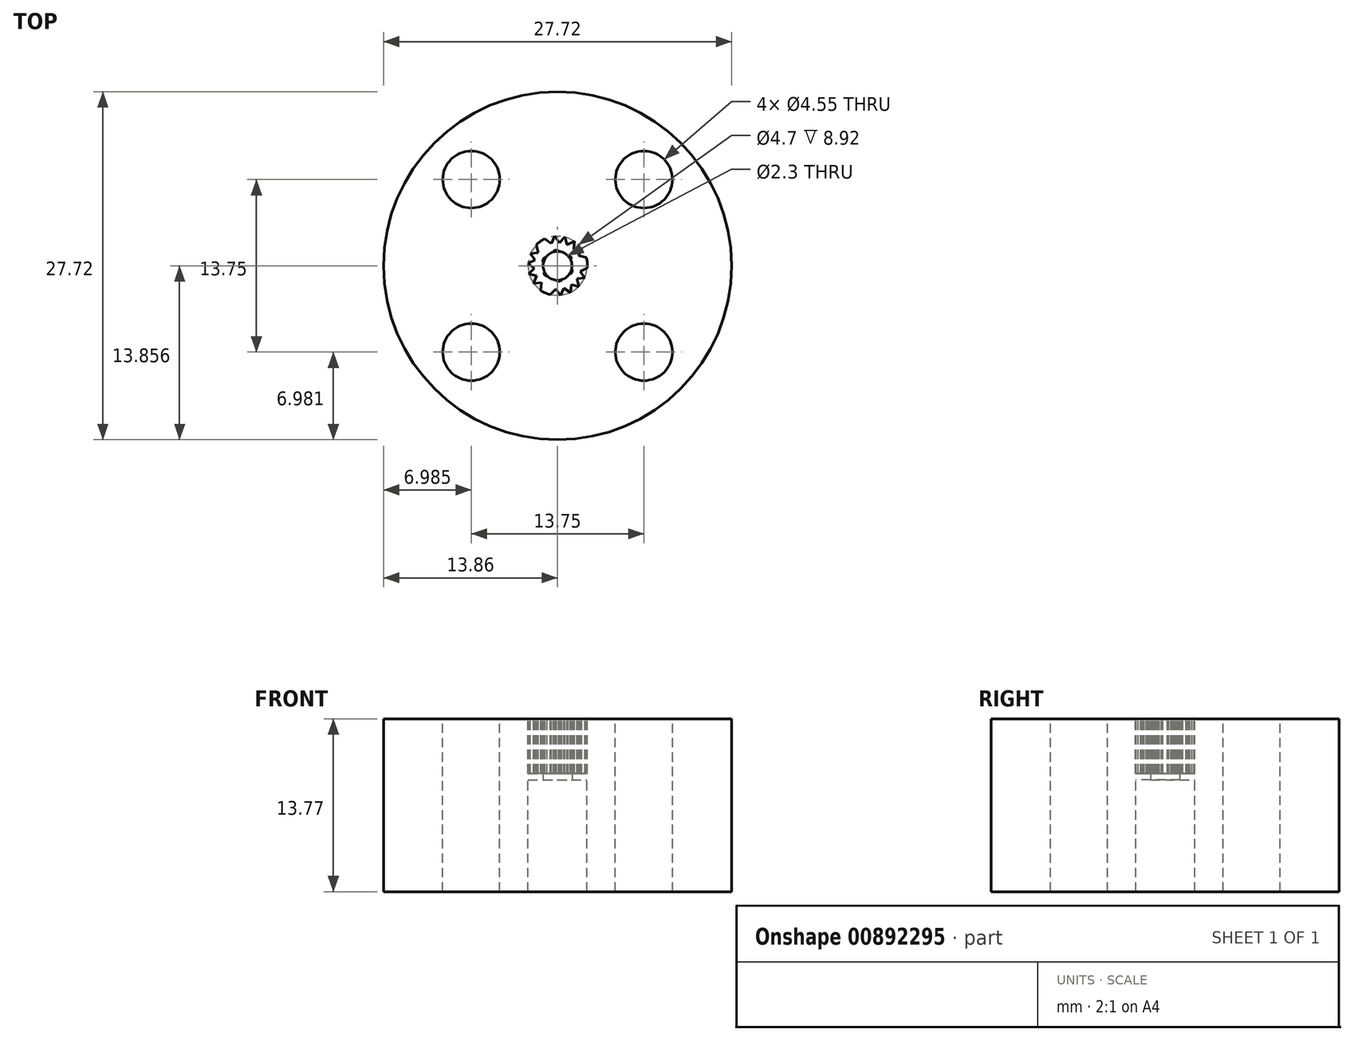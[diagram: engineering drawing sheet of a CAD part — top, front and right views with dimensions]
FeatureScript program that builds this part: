
annotation { "Feature Type Name" : "Feature", "Feature Type Description" : "" }
export const myFeature = defineFeature(function(context is Context, id is Id, definition is map)
    precondition{}
    {
        {
            var Q0;
            Q0=qCreatedBy(makeId("Top.planeOp"),FACE);
            var sketch = newSketch(context, id + "F0", { "sketchPlane" : qUnion([Q0])});
            skCircle(sketch, "E0", {"center": v(0, 2.4) * mm, "radius": 13.86 * mm});
            skSolve(sketch);
        }
        {
            var Q0;
            Q0 = qSketchRegion(id + "F0", true);
            extrude(context, id + "F1", {"entities" : qUnion([Q0]), "depth" : 13.77 * mm, "offsetDistance" : 25 * mm});
        }
        {
            var Q0;
            Q0=makeQuery(id+"F1.opExtrude","CAP_FACE",FACE,{"disambiguationData":[OSD([sQuery(id+"F0.wireOp",EDGE,"E0")])],"isStart":false});
            var sketch = newSketch(context, id + "F2", { "sketchPlane" : qUnion([Q0])});
            skCircle(sketch, "E1", {"center": v(0, 2.4) * mm, "radius": 2.35 * mm});
            skLineSegment(sketch, "E2", {"start": v(13.86, 2.4) * mm, "end": v(-13.86, 2.4) * mm, "construction": true});
            skLineSegment(sketch, "E3", {"start": v(0, 16.27) * mm, "end": v(0, -11.45) * mm, "construction": true});
            skLineSegment(sketch, "E4", {"start": v(0, 16.27) * mm, "end": v(13.86, 2.4) * mm, "construction": true});
            skLineSegment(sketch, "E5", {"start": v(6.93, 9.34) * mm, "end": v(0, 2.4) * mm, "construction": true});
            skCircle(sketch, "E6", {"center": v(6.87, 9.28) * mm, "radius": 2.27 * mm});
            skCircle(sketch, "E7.1.0", {"center": v(-6.88, 9.28) * mm, "radius": 2.27 * mm});
            skCircle(sketch, "E7.2.0", {"center": v(-6.87, -4.47) * mm, "radius": 2.27 * mm});
            skCircle(sketch, "E7.3.0", {"center": v(6.88, -4.47) * mm, "radius": 2.27 * mm});
            skSolve(sketch);
        }
        {
            var Q0;
            Q0 = qSketchRegion(id + "F2", true);
            extrude(context, id + "F3", {"entities" : qUnion([Q0]), "operationType" : NewBodyOperationType.REMOVE, "oppositeDirection" : true, "depth" : 25 * mm, "offsetDistance" : 25 * mm});
        }
        {
            var Q0;
            Q0=makeQuery(id+"F1.opExtrude","CAP_FACE",FACE,{"disambiguationData":[OSD([sQuery(id+"F0.wireOp",EDGE,"E0")])],"isStart":false});
            var sketch = newSketch(context, id + "F4", { "sketchPlane" : qUnion([Q0])});
            skCircle(sketch, "E8.0", {"center": v(0, 2.4) * mm, "radius": 2.35 * mm});
            skSolve(sketch);
        }
        {
            var Q0;
            Q0 = qSketchRegion(id + "F4", true);
            extrude(context, id + "F5", {"entities" : qUnion([Q0]), "operationType" : NewBodyOperationType.ADD, "oppositeDirection" : true, "depth" : 6.9 * mm, "offsetDistance" : 25 * mm});
        }
        {
            var Q0;
            Q0=makeQuery(id+"F5.boolean.opBoolean","MERGE",FACE,{"derivedFrom":[makeQuery(id+"F1.opExtrude","CAP_FACE",FACE,{"disambiguationData":[OSD([sQuery(id+"F0.wireOp",EDGE,"E0")])],"isStart":false}),makeQuery(id+"F5.opExtrude","CAP_FACE",FACE,{"disambiguationData":[OSD([sQuery(id+"F4.wireOp",EDGE,"E8.0")])],"isStart":true})]});
            var sketch = newSketch(context, id + "F6", { "sketchPlane" : qUnion([Q0])});
            skCircle(sketch, "E9", {"center": v(0, 2.4) * mm, "radius": 2.38 * mm});
            skCircle(sketch, "E10.cCircle", {"center": v(0, 2.4) * mm, "radius": 2.38 * mm, "construction": true});
            skLineSegment(sketch, "E10.0", {"start": v(-0.58, 0.1) * mm, "end": v(-1.7, 4.07) * mm});
            skLineSegment(sketch, "E10.1", {"start": v(-1.7, 4.07) * mm, "end": v(2.3, 3.05) * mm});
            skLineSegment(sketch, "E10.2", {"start": v(2.3, 3.05) * mm, "end": v(-0.58, 0.1) * mm});
            skLineSegment(sketch, "E11.1.0", {"start": v(2.37, 2.23) * mm, "end": v(-1.34, 0.44) * mm});
            skLineSegment(sketch, "E11.1.1", {"start": v(-1.34, 0.44) * mm, "end": v(-1.04, 4.55) * mm});
            skLineSegment(sketch, "E11.1.2", {"start": v(-1.04, 4.55) * mm, "end": v(2.37, 2.23) * mm});
            skLineSegment(sketch, "E11.2.0", {"start": v(2.17, 1.43) * mm, "end": v(-1.93, 1.01) * mm});
            skLineSegment(sketch, "E11.2.1", {"start": v(-1.93, 1.01) * mm, "end": v(-0.24, 4.77) * mm});
            skLineSegment(sketch, "E11.2.2", {"start": v(-0.24, 4.77) * mm, "end": v(2.17, 1.43) * mm});
            skLineSegment(sketch, "E11.3.0", {"start": v(1.7, 0.75) * mm, "end": v(-2.3, 1.76) * mm});
            skLineSegment(sketch, "E11.3.1", {"start": v(-2.3, 1.76) * mm, "end": v(0.58, 4.71) * mm});
            skLineSegment(sketch, "E11.3.2", {"start": v(0.58, 4.71) * mm, "end": v(1.7, 0.75) * mm});
            skLineSegment(sketch, "E11.4.0", {"start": v(1.04, 0.26) * mm, "end": v(-2.37, 2.58) * mm});
            skLineSegment(sketch, "E11.4.1", {"start": v(-2.37, 2.58) * mm, "end": v(1.34, 4.37) * mm});
            skLineSegment(sketch, "E11.4.2", {"start": v(1.34, 4.37) * mm, "end": v(1.04, 0.26) * mm});
            skLineSegment(sketch, "E11.5.0", {"start": v(0.24, 0.04) * mm, "end": v(-2.17, 3.38) * mm});
            skLineSegment(sketch, "E11.5.1", {"start": v(-2.17, 3.38) * mm, "end": v(1.93, 3.8) * mm});
            skLineSegment(sketch, "E11.5.2", {"start": v(1.93, 3.8) * mm, "end": v(0.24, 0.04) * mm});
            skLineSegment(sketch, "E11.7.0", {"start": v(-1.34, 0.44) * mm, "end": v(-1.04, 4.55) * mm});
            skLineSegment(sketch, "E11.7.1", {"start": v(-1.04, 4.55) * mm, "end": v(2.37, 2.23) * mm});
            skLineSegment(sketch, "E11.7.2", {"start": v(2.37, 2.23) * mm, "end": v(-1.34, 0.44) * mm});
            skLineSegment(sketch, "E11.anchor1", {"start": v(0, 2.4) * mm, "end": v(-0.58, 0.1) * mm, "construction": true});
            skLineSegment(sketch, "E11.anchor2", {"start": v(0, 2.4) * mm, "end": v(-1.04, 4.55) * mm, "construction": true});
            skSolve(sketch);
        }
        {
            var Q0;
            Q0=makeQuery(id+"F6.imprint","IMPRINT",FACE,{"disambiguationData":[TD([[makeQuery(id+"F6.imprint","IMPRINT",EDGE,{"derivedFrom":makeQuery(id+"F1.opExtrude","CAP_EDGE",EDGE,{"disambiguationData":[OSD([sQuery(id+"F0.wireOp",EDGE,"E0")])],"isStart":false})}),1.0]])]});
            var sketch = newSketch(context, id + "F7", { "sketchPlane" : qUnion([Q0])});
            skCircle(sketch, "E12.0", {"center": v(0, 2.4) * mm, "radius": 2.38 * mm});
            skSolve(sketch);
        }
        {
            var Q0;
            Q0 = qSketchRegion(id + "F7", true);
            extrude(context, id + "F8", {"entities" : qUnion([Q0]), "operationType" : NewBodyOperationType.REMOVE, "oppositeDirection" : true, "depth" : 4.35 * mm, "offsetDistance" : 25 * mm});
        }
        {
            var Q0;
            {var subQ0=sQuery(id+"F6.wireOp",EDGE,"E11.4.2");var subQ3=sQuery(id+"F6.wireOp",EDGE,"E11.5.1");var subQ5=makeQuery(id+"F6.imprint","INTERSECT",VERTEX,{"derivedFrom":[subQ0,subQ3]});Q0=makeQuery(id+"F6.imprint","IMPRINT",FACE,{"disambiguationData":[TD([[makeQuery(id+"F6.imprint","IMPRINT",EDGE,{"disambiguationData":[TD([[subQ5,1.0]])],"derivedFrom":subQ0}),1.0]])]});}
            var Q1;
            {var subQ0=sQuery(id+"F6.wireOp",EDGE,"E11.5.2");var subQ3=sQuery(id+"F6.wireOp",EDGE,"E10.1");var subQ5=makeQuery(id+"F6.imprint","INTERSECT",VERTEX,{"derivedFrom":[subQ0,subQ3]});Q1=makeQuery(id+"F6.imprint","IMPRINT",FACE,{"disambiguationData":[TD([[makeQuery(id+"F6.imprint","IMPRINT",EDGE,{"disambiguationData":[TD([[subQ5,1.0]])],"derivedFrom":subQ0}),1.0]])]});}
            var Q2;
            {var subQ0=sQuery(id+"F6.wireOp",EDGE,"E10.2");var subQ3=sQuery(id+"F6.wireOp",EDGE,"E11.7.1");var subQ5=makeQuery(id+"F6.imprint","INTERSECT",VERTEX,{"derivedFrom":[subQ0,subQ3]});Q2=makeQuery(id+"F6.imprint","IMPRINT",FACE,{"disambiguationData":[TD([[makeQuery(id+"F6.imprint","IMPRINT",EDGE,{"disambiguationData":[TD([[subQ5,1.0]])],"derivedFrom":subQ0}),1.0]])]});}
            var Q3;
            {var subQ0=sQuery(id+"F6.wireOp",EDGE,"E11.2.2");var subQ3=sQuery(id+"F6.wireOp",EDGE,"E11.7.2");var subQ5=makeQuery(id+"F6.imprint","INTERSECT",VERTEX,{"derivedFrom":[subQ0,subQ3]});Q3=makeQuery(id+"F6.imprint","IMPRINT",FACE,{"disambiguationData":[TD([[makeQuery(id+"F6.imprint","IMPRINT",EDGE,{"disambiguationData":[TD([[subQ5,-1.0]])],"derivedFrom":subQ0}),1.0]])]});}
            var Q4;
            {var subQ0=sQuery(id+"F6.wireOp",EDGE,"E11.2.0");var subQ3=sQuery(id+"F6.wireOp",EDGE,"E11.3.2");var subQ5=makeQuery(id+"F6.imprint","INTERSECT",VERTEX,{"derivedFrom":[subQ0,subQ3]});Q4=makeQuery(id+"F6.imprint","IMPRINT",FACE,{"disambiguationData":[TD([[makeQuery(id+"F6.imprint","IMPRINT",EDGE,{"disambiguationData":[TD([[subQ5,1.0]])],"derivedFrom":subQ0}),1.0]])]});}
            var Q5;
            {var subQ0=sQuery(id+"F6.wireOp",EDGE,"E11.3.0");var subQ3=sQuery(id+"F6.wireOp",EDGE,"E11.4.2");var subQ5=makeQuery(id+"F6.imprint","INTERSECT",VERTEX,{"derivedFrom":[subQ0,subQ3]});Q5=makeQuery(id+"F6.imprint","IMPRINT",FACE,{"disambiguationData":[TD([[makeQuery(id+"F6.imprint","IMPRINT",EDGE,{"disambiguationData":[TD([[subQ5,1.0]])],"derivedFrom":subQ0}),1.0]])]});}
            var Q6;
            {var subQ0=sQuery(id+"F6.wireOp",EDGE,"E11.4.0");var subQ3=sQuery(id+"F6.wireOp",EDGE,"E11.5.2");var subQ5=makeQuery(id+"F6.imprint","INTERSECT",VERTEX,{"derivedFrom":[subQ0,subQ3]});Q6=makeQuery(id+"F6.imprint","IMPRINT",FACE,{"disambiguationData":[TD([[makeQuery(id+"F6.imprint","IMPRINT",EDGE,{"disambiguationData":[TD([[subQ5,1.0]])],"derivedFrom":subQ0}),1.0]])]});}
            var Q7;
            {var subQ0=sQuery(id+"F6.wireOp",EDGE,"E11.5.0");var subQ3=sQuery(id+"F6.wireOp",EDGE,"E10.2");var subQ5=makeQuery(id+"F6.imprint","INTERSECT",VERTEX,{"derivedFrom":[subQ0,subQ3]});Q7=makeQuery(id+"F6.imprint","IMPRINT",FACE,{"disambiguationData":[TD([[makeQuery(id+"F6.imprint","IMPRINT",EDGE,{"disambiguationData":[TD([[subQ5,1.0]])],"derivedFrom":subQ0}),1.0]])]});}
            var Q8;
            {var subQ0=sQuery(id+"F6.wireOp",EDGE,"E10.0");var subQ3=sQuery(id+"F6.wireOp",EDGE,"E11.7.2");var subQ5=makeQuery(id+"F6.imprint","INTERSECT",VERTEX,{"derivedFrom":[subQ0,subQ3]});Q8=makeQuery(id+"F6.imprint","IMPRINT",FACE,{"disambiguationData":[TD([[makeQuery(id+"F6.imprint","IMPRINT",EDGE,{"disambiguationData":[TD([[subQ5,1.0]])],"derivedFrom":subQ0}),1.0]])]});}
            var Q9;
            {var subQ0=sQuery(id+"F6.wireOp",EDGE,"E11.2.0");var subQ3=sQuery(id+"F6.wireOp",EDGE,"E11.7.0");var subQ5=makeQuery(id+"F6.imprint","INTERSECT",VERTEX,{"derivedFrom":[subQ0,subQ3]});Q9=makeQuery(id+"F6.imprint","IMPRINT",FACE,{"disambiguationData":[TD([[makeQuery(id+"F6.imprint","IMPRINT",EDGE,{"disambiguationData":[TD([[subQ5,-1.0]])],"derivedFrom":subQ0}),1.0]])]});}
            var Q10;
            {var subQ0=sQuery(id+"F6.wireOp",EDGE,"E11.2.1");var subQ3=sQuery(id+"F6.wireOp",EDGE,"E11.3.0");var subQ5=makeQuery(id+"F6.imprint","INTERSECT",VERTEX,{"derivedFrom":[subQ0,subQ3]});Q10=makeQuery(id+"F6.imprint","IMPRINT",FACE,{"disambiguationData":[TD([[makeQuery(id+"F6.imprint","IMPRINT",EDGE,{"disambiguationData":[TD([[subQ5,1.0]])],"derivedFrom":subQ0}),1.0]])]});}
            var Q11;
            {var subQ0=sQuery(id+"F6.wireOp",EDGE,"E11.3.1");var subQ3=sQuery(id+"F6.wireOp",EDGE,"E11.4.0");var subQ5=makeQuery(id+"F6.imprint","INTERSECT",VERTEX,{"derivedFrom":[subQ0,subQ3]});Q11=makeQuery(id+"F6.imprint","IMPRINT",FACE,{"disambiguationData":[TD([[makeQuery(id+"F6.imprint","IMPRINT",EDGE,{"disambiguationData":[TD([[subQ5,1.0]])],"derivedFrom":subQ0}),1.0]])]});}
            var Q12;
            {var subQ0=sQuery(id+"F6.wireOp",EDGE,"E11.4.1");var subQ3=sQuery(id+"F6.wireOp",EDGE,"E11.5.0");var subQ5=makeQuery(id+"F6.imprint","INTERSECT",VERTEX,{"derivedFrom":[subQ0,subQ3]});Q12=makeQuery(id+"F6.imprint","IMPRINT",FACE,{"disambiguationData":[TD([[makeQuery(id+"F6.imprint","IMPRINT",EDGE,{"disambiguationData":[TD([[subQ5,1.0]])],"derivedFrom":subQ0}),1.0]])]});}
            var Q13;
            {var subQ0=sQuery(id+"F6.wireOp",EDGE,"E11.5.1");var subQ3=sQuery(id+"F6.wireOp",EDGE,"E10.0");var subQ5=makeQuery(id+"F6.imprint","INTERSECT",VERTEX,{"derivedFrom":[subQ0,subQ3]});Q13=makeQuery(id+"F6.imprint","IMPRINT",FACE,{"disambiguationData":[TD([[makeQuery(id+"F6.imprint","IMPRINT",EDGE,{"disambiguationData":[TD([[subQ5,1.0]])],"derivedFrom":subQ0}),1.0]])]});}
            var Q14;
            {var subQ0=sQuery(id+"F6.wireOp",EDGE,"E10.1");var subQ3=sQuery(id+"F6.wireOp",EDGE,"E11.7.0");var subQ5=makeQuery(id+"F6.imprint","INTERSECT",VERTEX,{"derivedFrom":[subQ0,subQ3]});Q14=makeQuery(id+"F6.imprint","IMPRINT",FACE,{"disambiguationData":[TD([[makeQuery(id+"F6.imprint","IMPRINT",EDGE,{"disambiguationData":[TD([[subQ5,1.0]])],"derivedFrom":subQ0}),1.0]])]});}
            var Q15;
            {var subQ0=sQuery(id+"F6.wireOp",EDGE,"E11.2.1");var subQ3=sQuery(id+"F6.wireOp",EDGE,"E11.7.1");var subQ5=makeQuery(id+"F6.imprint","INTERSECT",VERTEX,{"derivedFrom":[subQ0,subQ3]});Q15=makeQuery(id+"F6.imprint","IMPRINT",FACE,{"disambiguationData":[TD([[makeQuery(id+"F6.imprint","IMPRINT",EDGE,{"disambiguationData":[TD([[subQ5,-1.0]])],"derivedFrom":subQ0}),1.0]])]});}
            var Q16;
            {var subQ0=sQuery(id+"F6.wireOp",EDGE,"E11.2.2");var subQ3=sQuery(id+"F6.wireOp",EDGE,"E11.3.1");var subQ5=makeQuery(id+"F6.imprint","INTERSECT",VERTEX,{"derivedFrom":[subQ0,subQ3]});Q16=makeQuery(id+"F6.imprint","IMPRINT",FACE,{"disambiguationData":[TD([[makeQuery(id+"F6.imprint","IMPRINT",EDGE,{"disambiguationData":[TD([[subQ5,1.0]])],"derivedFrom":subQ0}),1.0]])]});}
            var Q17;
            {var subQ0=sQuery(id+"F6.wireOp",EDGE,"E11.3.2");var subQ3=sQuery(id+"F6.wireOp",EDGE,"E11.4.1");var subQ5=makeQuery(id+"F6.imprint","INTERSECT",VERTEX,{"derivedFrom":[subQ0,subQ3]});Q17=makeQuery(id+"F6.imprint","IMPRINT",FACE,{"disambiguationData":[TD([[makeQuery(id+"F6.imprint","IMPRINT",EDGE,{"disambiguationData":[TD([[subQ5,1.0]])],"derivedFrom":subQ0}),1.0]])]});}
            extrude(context, id + "F9", {"entities" : qUnion([Q0, Q1, Q2, Q3, Q4, Q5, Q6, Q7, Q8, Q9, Q10, Q11, Q12, Q13, Q14, Q15, Q16, Q17]), "operationType" : NewBodyOperationType.ADD, "oppositeDirection" : true, "depth" : 5 * mm, "offsetDistance" : 25 * mm});
        }
        {
            var Q0;
            Q0=makeQuery(id+"F5.opExtrude","CAP_FACE",FACE,{"disambiguationData":[OSD([sQuery(id+"F4.wireOp",EDGE,"E8.0")])],"isStart":false});
            var sketch = newSketch(context, id + "F10", { "sketchPlane" : qUnion([Q0])});
            skCircle(sketch, "E13", {"center": v(0, -2.4) * mm, "radius": 1.15 * mm});
            skSolve(sketch);
        }
        {
            var Q0;
            Q0 = qSketchRegion(id + "F10", true);
            extrude(context, id + "F11", {"entities" : qUnion([Q0]), "operationType" : NewBodyOperationType.REMOVE, "oppositeDirection" : true, "depth" : 25 * mm, "offsetDistance" : 25 * mm});
        }
        {
            var Q0;
            Q0=makeQuery(id+"F8.boolean.opBoolean","COPY",FACE,{"derivedFrom":makeQuery(id+"F8.opExtrude","CAP_FACE",FACE,{"disambiguationData":[OSD([sQuery(id+"F7.wireOp",EDGE,"E12.0")])],"isStart":false})});
            var sketch = newSketch(context, id + "F12", { "sketchPlane" : qUnion([Q0])});
            skCircle(sketch, "E14", {"center": v(0, 2.4) * mm, "radius": 2.35 * mm});
            skSolve(sketch);
        }
        {
            var Q0;
            Q0 = qSketchRegion(id + "F12", true);
            extrude(context, id + "F13", {"entities" : qUnion([Q0]), "operationType" : NewBodyOperationType.REMOVE, "oppositeDirection" : true, "depth" : 25 * mm, "offsetDistance" : 25 * mm});
        }
        {
            var Q0;
            {var subQ0=sQuery(id+"F6.wireOp",EDGE,"E10.1");var subQ2=sQuery(id+"F6.wireOp",EDGE,"E11.5.2");var subQ3=makeQuery(id+"F6.imprint","INTERSECT",VERTEX,{"derivedFrom":[subQ2,subQ0]});var subQ4=sQuery(id+"F12.wireOp",EDGE,"E14");Q0=makeQuery(id+"F13.boolean.opBoolean","COPY",FACE,{"disambiguationData":[TD([makeQuery(id+"F9.opExtrude","SWEPT_FACE",FACE,{"disambiguationData":[OSD([subQ2]),TDD([makeQuery(id+"F6.imprint","IMPRINT",EDGE,{"disambiguationData":[TD([[subQ3,1.0]])],"derivedFrom":subQ2})])]})])],"derivedFrom":makeQuery(id+"F13.opExtrude","CAP_FACE",FACE,{"disambiguationData":[OSD([subQ4])],"isStart":true})});}
            var sketch = newSketch(context, id + "F14", { "sketchPlane" : qUnion([Q0])});
            skCircle(sketch, "E15.0", {"center": v(0, -2.4) * mm, "radius": 2.35 * mm});
            skSolve(sketch);
        }
        {
            var Q0;
            Q0 = qSketchRegion(id + "F14", true);
            extrude(context, id + "F15", {"entities" : qUnion([Q0]), "operationType" : NewBodyOperationType.ADD, "depth" : .5 * mm, "offsetDistance" : 25 * mm});
        }
        {
            var Q0;
            Q0=makeQuery(id+"F15.opExtrude","CAP_FACE",FACE,{"disambiguationData":[OSD([sQuery(id+"F14.wireOp",EDGE,"E15.0")])],"isStart":false});
            var sketch = newSketch(context, id + "F16", { "sketchPlane" : qUnion([Q0])});
            skCircle(sketch, "E16", {"center": v(0, -2.4) * mm, "radius": 1.15 * mm});
            skSolve(sketch);
        }
        {
            var Q0;
            Q0 = qSketchRegion(id + "F16", true);
            extrude(context, id + "F17", {"entities" : qUnion([Q0]), "operationType" : NewBodyOperationType.REMOVE, "oppositeDirection" : true, "depth" : 25 * mm, "offsetDistance" : 25 * mm});
        }
    });
